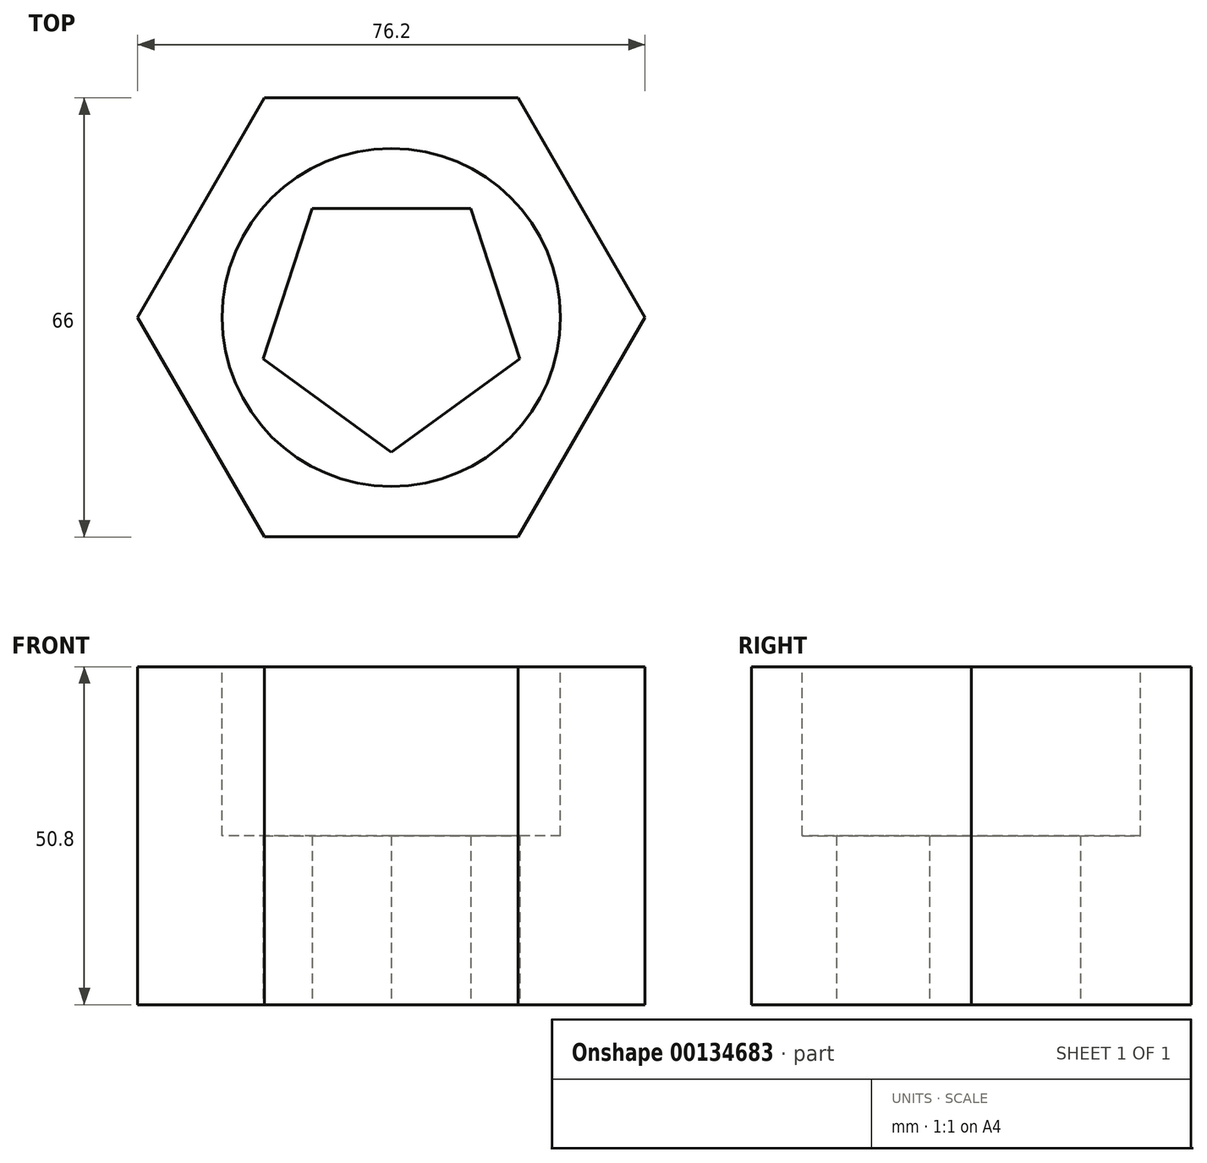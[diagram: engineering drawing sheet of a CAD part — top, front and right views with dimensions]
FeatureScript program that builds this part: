
annotation { "Feature Type Name" : "Feature", "Feature Type Description" : "" }
export const myFeature = defineFeature(function(context is Context, id is Id, definition is map)
    precondition{}
    {
        {
            var Q0;
            Q0=qCreatedBy(makeId("Top.planeOp"),FACE);
            var sketch = newSketch(context, id + "F0", { "sketchPlane" : qUnion([Q0])});
            skCircle(sketch, "E0.cCircle", {"center": v(0, 0) * mm, "radius": 33 * mm, "construction": true});
            skLineSegment(sketch, "E0.0", {"start": v(-19.05, 33) * mm, "end": v(19.05, 33) * mm});
            skLineSegment(sketch, "E0.1", {"start": v(19.05, 33) * mm, "end": v(38.1, 0) * mm});
            skLineSegment(sketch, "E0.2", {"start": v(38.1, 0) * mm, "end": v(19.05, -33) * mm});
            skLineSegment(sketch, "E0.3", {"start": v(19.05, -33) * mm, "end": v(-19.05, -33) * mm});
            skLineSegment(sketch, "E0.4", {"start": v(-19.05, -33) * mm, "end": v(-38.1, 0) * mm});
            skLineSegment(sketch, "E0.5", {"start": v(-38.1, 0) * mm, "end": v(-19.05, 33) * mm});
            skPoint(sketch, "E0.0.midPoint", {"position": v(0, 33) * mm});
            skCircle(sketch, "E1.cCircle", {"center": v(0, 0) * mm, "radius": 16.39 * mm, "construction": true});
            skLineSegment(sketch, "E1.0", {"start": v(-11.9, 16.39) * mm, "end": v(11.9, 16.39) * mm});
            skLineSegment(sketch, "E1.1", {"start": v(11.9, 16.39) * mm, "end": v(19.26, -6.26) * mm});
            skLineSegment(sketch, "E1.2", {"start": v(19.26, -6.26) * mm, "end": v(0, -20.26) * mm});
            skLineSegment(sketch, "E1.3", {"start": v(0, -20.26) * mm, "end": v(-19.26, -6.26) * mm});
            skLineSegment(sketch, "E1.4", {"start": v(-19.26, -6.26) * mm, "end": v(-11.9, 16.39) * mm});
            skPoint(sketch, "E1.0.midPoint", {"position": v(0, 16.39) * mm});
            skSolve(sketch);
        }
        {
            var Q0;
            Q0=makeQuery(id+"F0.imprint","IMPRINT",FACE,{"disambiguationData":[TD([[makeQuery(id+"F0.imprint","IMPRINT",EDGE,{"derivedFrom":sQuery(id+"F0.wireOp",EDGE,"E0.0")}),-1.0]])]});
            extrude(context, id + "F1", {"entities" : qUnion([Q0]), "depth" : 25.4 * mm});
        }
        {
            var Q0;
            Q0=makeQuery(id+"F1.opExtrude","CAP_FACE",FACE,{"disambiguationData":[OSD([sQuery(id+"F0.wireOp",EDGE,"E0.0"),sQuery(id+"F0.wireOp",EDGE,"E0.1"),sQuery(id+"F0.wireOp",EDGE,"E0.2"),sQuery(id+"F0.wireOp",EDGE,"E0.3"),sQuery(id+"F0.wireOp",EDGE,"E0.4"),sQuery(id+"F0.wireOp",EDGE,"E0.5"),sQuery(id+"F0.wireOp",EDGE,"E1.0"),sQuery(id+"F0.wireOp",EDGE,"E1.1"),sQuery(id+"F0.wireOp",EDGE,"E1.2"),sQuery(id+"F0.wireOp",EDGE,"E1.3"),sQuery(id+"F0.wireOp",EDGE,"E1.4")])],"isStart":false});
            var sketch = newSketch(context, id + "F2", { "sketchPlane" : qUnion([Q0])});
            skLineSegment(sketch, "E2.0", {"start": v(38.1, 0) * mm, "end": v(19.05, -33) * mm});
            skLineSegment(sketch, "E3.0", {"start": v(19.05, -33) * mm, "end": v(-19.05, -33) * mm});
            skLineSegment(sketch, "E4.0", {"start": v(-19.05, -33) * mm, "end": v(-38.1, 0) * mm});
            skLineSegment(sketch, "E5.0", {"start": v(-38.1, 0) * mm, "end": v(-19.05, 33) * mm});
            skLineSegment(sketch, "E6.0", {"start": v(-19.05, 33) * mm, "end": v(19.05, 33) * mm});
            skLineSegment(sketch, "E7.0", {"start": v(19.05, 33) * mm, "end": v(38.1, 0) * mm});
            skSolve(sketch);
        }
        {
            var Q0;
            Q0=makeQuery(id+"F2.imprint","IMPRINT",FACE,{"disambiguationData":[TD([[makeQuery(id+"F2.imprint","IMPRINT",EDGE,{"derivedFrom":makeQuery(id+"F1.opExtrude","CAP_EDGE",EDGE,{"disambiguationData":[OSD([sQuery(id+"F0.wireOp",EDGE,"E1.0")])],"isStart":false})}),-1.0]])]});
            var Q1;
            Q1=makeQuery(id+"F2.imprint","IMPRINT",FACE,{"disambiguationData":[TD([[makeQuery(id+"F2.imprint","IMPRINT",EDGE,{"derivedFrom":sQuery(id+"F2.wireOp",EDGE,"E2.0")}),-1.0]])]});
            extrude(context, id + "F3", {"entities" : qUnion([Q0, Q1]), "operationType" : NewBodyOperationType.ADD, "depth" : 25.4 * mm});
        }
        {
            var Q0;
            Q0=makeQuery(id+"F3.opExtrude","CAP_FACE",FACE,{"disambiguationData":[OSD([sQuery(id+"F2.wireOp",EDGE,"E2.0"),sQuery(id+"F2.wireOp",EDGE,"E3.0"),sQuery(id+"F2.wireOp",EDGE,"E4.0"),sQuery(id+"F2.wireOp",EDGE,"E5.0"),sQuery(id+"F2.wireOp",EDGE,"E6.0"),sQuery(id+"F2.wireOp",EDGE,"E7.0")])],"isStart":false});
            var sketch = newSketch(context, id + "F4", { "sketchPlane" : qUnion([Q0])});
            skCircle(sketch, "E8", {"center": v(0, 0) * mm, "radius": 25.4 * mm});
            skSolve(sketch);
        }
        {
            var Q0;
            Q0=makeQuery(id+"F4.imprint","IMPRINT",FACE,{"disambiguationData":[TD([[makeQuery(id+"F4.imprint","IMPRINT",EDGE,{"derivedFrom":sQuery(id+"F4.wireOp",EDGE,"E8")}),1.0]])]});
            extrude(context, id + "F5", {"entities" : qUnion([Q0]), "operationType" : NewBodyOperationType.REMOVE, "oppositeDirection" : true, "depth" : 25.4 * mm});
        }
    });
